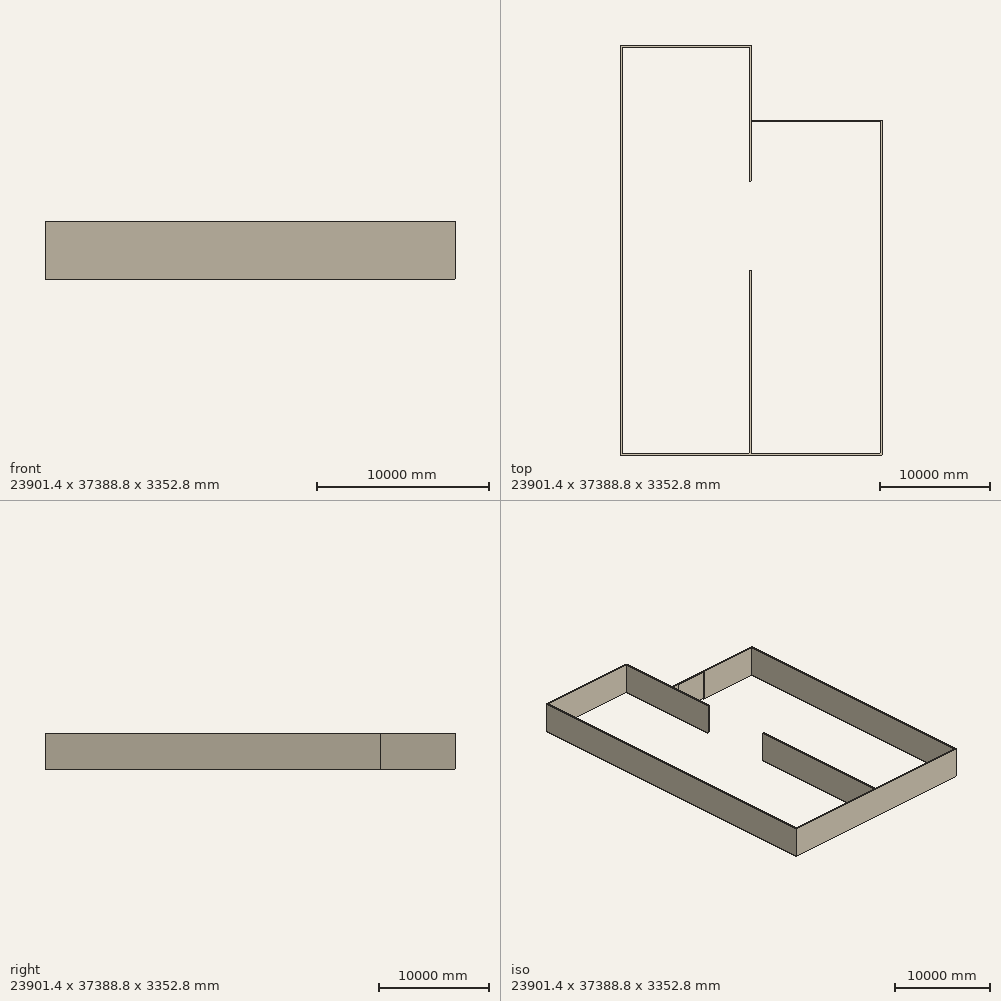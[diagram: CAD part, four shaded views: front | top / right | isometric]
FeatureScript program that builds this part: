
annotation { "Feature Type Name" : "Feature", "Feature Type Description" : "" }
export const myFeature = defineFeature(function(context is Context, id is Id, definition is map)
    precondition{}
    {
        {
            var Q0;
            Q0=qCreatedBy(makeId("Top.planeOp"),FACE);
            var sketch = newSketch(context, id + "F0", { "sketchPlane" : qUnion([Q0])});
            skLineSegment(sketch, "E0", {"start": v(-11355.72, 18524.11) * mm, "end": v(-11355.72, -18864.69) * mm});
            skLineSegment(sketch, "E1", {"start": v(-11355.72, -18864.69) * mm, "end": v(12545.68, -18864.69) * mm});
            skLineSegment(sketch, "E2", {"start": v(12545.68, -18864.69) * mm, "end": v(12545.68, 11716.91) * mm});
            skLineSegment(sketch, "E3", {"start": v(12545.68, 11716.91) * mm, "end": v(556.88, 11716.91) * mm});
            skLineSegment(sketch, "E4", {"start": v(556.88, 11716.91) * mm, "end": v(556.88, 18524.11) * mm});
            skLineSegment(sketch, "E5", {"start": v(556.88, 18524.11) * mm, "end": v(-11355.72, 18524.11) * mm});
            skLineSegment(sketch, "E6", {"start": v(556.88, 11716.91) * mm, "end": v(556.88, 6128.91) * mm});
            skLineSegment(sketch, "E7", {"start": v(556.88, -18864.69) * mm, "end": v(556.88, -2024.49) * mm});
            skPoint(sketch, "E7.startSnap0", {"position": v(594.98, -18864.69) * mm});
            skLineSegment(sketch, "E8.0", {"start": v(-11203.32, -18712.29) * mm, "end": v(12393.28, -18712.29) * mm});
            skLineSegment(sketch, "E8.1", {"start": v(12393.28, 11564.51) * mm, "end": v(404.48, 11564.51) * mm});
            skLineSegment(sketch, "E8.2", {"start": v(404.48, 11564.51) * mm, "end": v(404.48, 18371.71) * mm});
            skLineSegment(sketch, "E8.3", {"start": v(12393.28, -18712.29) * mm, "end": v(12393.28, 11564.51) * mm});
            skLineSegment(sketch, "E8.4", {"start": v(404.48, 18371.71) * mm, "end": v(-11203.32, 18371.71) * mm});
            skLineSegment(sketch, "E8.5", {"start": v(-11203.32, 18371.71) * mm, "end": v(-11203.32, -18712.29) * mm});
            skLineSegment(sketch, "E9.0", {"start": v(404.48, 11716.91) * mm, "end": v(404.48, 6128.91) * mm});
            skLineSegment(sketch, "E10.0", {"start": v(404.48, -18864.69) * mm, "end": v(404.48, -2024.49) * mm});
            skLineSegment(sketch, "E11", {"start": v(556.88, 6128.91) * mm, "end": v(404.48, 6128.91) * mm});
            skLineSegment(sketch, "E12", {"start": v(556.88, -2024.49) * mm, "end": v(404.48, -2024.49) * mm});
            skSolve(sketch);
        }
        {
            var Q0;
            {var subQ7=sQuery(id+"F0.wireOp",EDGE,"E0");Q0=makeQuery(id+"F0.imprint","IMPRINT",FACE,{"disambiguationData":[TD([[makeQuery(id+"F0.imprint","IMPRINT",EDGE,{"derivedFrom":subQ7}),1.0]])]});}
            var Q1;
            {var subQ0=sQuery(id+"F0.wireOp",EDGE,"E12");Q1=makeQuery(id+"F0.imprint","IMPRINT",FACE,{"disambiguationData":[TD([[makeQuery(id+"F0.imprint","IMPRINT",EDGE,{"derivedFrom":subQ0}),1.0]])]});}
            var Q2;
            {var subQ0=sQuery(id+"F0.wireOp",EDGE,"E11");Q2=makeQuery(id+"F0.imprint","IMPRINT",FACE,{"disambiguationData":[TD([[makeQuery(id+"F0.imprint","IMPRINT",EDGE,{"derivedFrom":subQ0}),-1.0]])]});}
            var Q3;
            {var subQ1=sQuery(id+"F0.wireOp",EDGE,"E2");Q3=makeQuery(id+"F0.imprint","IMPRINT",FACE,{"disambiguationData":[TD([[makeQuery(id+"F0.imprint","IMPRINT",EDGE,{"derivedFrom":subQ1}),1.0]])]});}
            var Q4;
            {var subQ0=sQuery(id+"F0.wireOp",EDGE,"E7");var subQ1=sQuery(id+"F0.wireOp",EDGE,"E1");var subQ2=makeQuery(id+"F0.imprint","INTERSECT",VERTEX,{"derivedFrom":[subQ1,subQ0]});Q4=makeQuery(id+"F0.imprint","IMPRINT",FACE,{"disambiguationData":[TD([[makeQuery(id+"F0.imprint","IMPRINT",EDGE,{"disambiguationData":[TD([[subQ2,1.0]])],"derivedFrom":subQ1}),1.0]])]});}
            extrude(context, id + "F1", {"entities" : qUnion([Q0, Q1, Q2, Q3, Q4]), "depth" : 3352.8 * mm, "offsetDistance" : 25.4 * mm});
        }
        {
            var Q0;
            Q0=makeQuery(id+"F1.opExtrude","SWEPT_FACE",FACE,{"disambiguationData":[OSD([sQuery(id+"F0.wireOp",EDGE,"E8.1")])]});
            var sketch = newSketch(context, id + "F2", { "sketchPlane" : qUnion([Q0])});
            skLineSegment(sketch, "E13.bottom", {"start": v(1381.76, 3251.2) * mm, "end": v(5229.86, 3251.2) * mm});
            skLineSegment(sketch, "E13.top", {"start": v(1381.76, 0) * mm, "end": v(5229.86, 0) * mm});
            skLineSegment(sketch, "E13.left", {"start": v(1381.76, 3251.2) * mm, "end": v(1381.76, 0) * mm});
            skLineSegment(sketch, "E13.right", {"start": v(5229.86, 3251.2) * mm, "end": v(5229.86, 0) * mm});
            skSolve(sketch);
        }
        {
            var Q0;
            Q0=makeQuery(id+"F2.imprint","IMPRINT",FACE,{"disambiguationData":[TD([[makeQuery(id+"F2.imprint","IMPRINT",EDGE,{"derivedFrom":sQuery(id+"F2.wireOp",EDGE,"E13.bottom")}),-1.0]])]});
            extrude(context, id + "F3", {"entities" : qUnion([Q0]), "operationType" : NewBodyOperationType.REMOVE, "oppositeDirection" : true, "depth" : 127 * mm, "offsetDistance" : 25.4 * mm});
        }
    });
